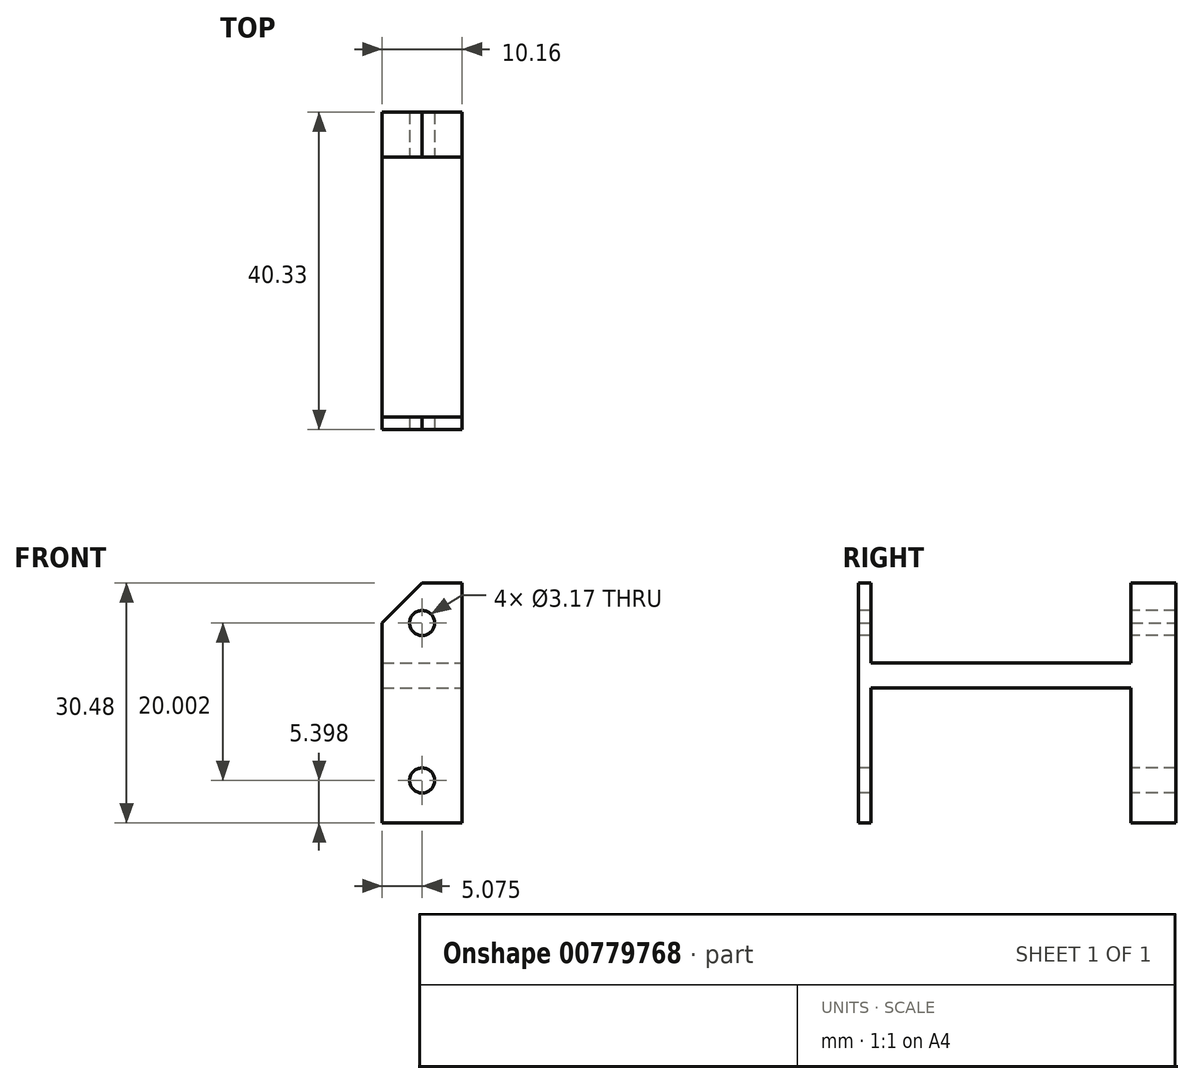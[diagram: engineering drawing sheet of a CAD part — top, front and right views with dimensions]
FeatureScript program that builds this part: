
annotation { "Feature Type Name" : "Feature", "Feature Type Description" : "" }
export const myFeature = defineFeature(function(context is Context, id is Id, definition is map)
    precondition{}
    {
        {
            var Q0;
            Q0=qCreatedBy(makeId("Front.planeOp"),FACE);
            var sketch = newSketch(context, id + "F0", { "sketchPlane" : qUnion([Q0])});
            skLineSegment(sketch, "E0", {"start": v(-16.21, 9.2) * mm, "end": v(-16.21, -16.2) * mm});
            skLineSegment(sketch, "E1", {"start": v(-16.21, -16.2) * mm, "end": v(-6.05, -16.2) * mm});
            skLineSegment(sketch, "E2", {"start": v(-6.05, -16.2) * mm, "end": v(-6.05, 14.27) * mm});
            skLineSegment(sketch, "E3", {"start": v(-6.05, 14.27) * mm, "end": v(-11.13, 14.27) * mm});
            skLineSegment(sketch, "E4", {"start": v(-11.13, 14.27) * mm, "end": v(-16.21, 9.2) * mm});
            skSolve(sketch);
        }
        {
            var Q0;
            Q0=makeQuery(id+"F0.imprint","IMPRINT",FACE,{"disambiguationData":[TD([[makeQuery(id+"F0.imprint","IMPRINT",EDGE,{"derivedFrom":sQuery(id+"F0.wireOp",EDGE,"E0")}),1.0]])]});
            extrude(context, id + "F1", {"entities" : qUnion([Q0]), "depth" : 1.59 * mm, "offsetDistance" : 25.4 * mm});
        }
        {
            var Q0;
            Q0=makeQuery(id+"F1.opExtrude","CAP_FACE",FACE,{"disambiguationData":[OSD([sQuery(id+"F0.wireOp",EDGE,"E0"),sQuery(id+"F0.wireOp",EDGE,"E1"),sQuery(id+"F0.wireOp",EDGE,"E2"),sQuery(id+"F0.wireOp",EDGE,"E3"),sQuery(id+"F0.wireOp",EDGE,"E4")])],"isStart":false});
            var sketch = newSketch(context, id + "F2", { "sketchPlane" : qUnion([Q0])});
            skLineSegment(sketch, "E5.bottom", {"start": v(-16.21, 4.11) * mm, "end": v(-6.05, 4.11) * mm});
            skLineSegment(sketch, "E5.top", {"start": v(-16.21, 0.94) * mm, "end": v(-6.05, 0.94) * mm});
            skLineSegment(sketch, "E5.left", {"start": v(-16.21, 4.11) * mm, "end": v(-16.21, 0.94) * mm});
            skLineSegment(sketch, "E5.right", {"start": v(-6.05, 4.11) * mm, "end": v(-6.05, 0.94) * mm});
            skSolve(sketch);
        }
        {
            var Q0;
            Q0=makeQuery(id+"F2.imprint","IMPRINT",FACE,{"disambiguationData":[TD([[makeQuery(id+"F2.imprint","IMPRINT",EDGE,{"derivedFrom":sQuery(id+"F2.wireOp",EDGE,"E5.bottom")}),-1.0]])]});
            extrude(context, id + "F3", {"entities" : qUnion([Q0]), "operationType" : NewBodyOperationType.ADD, "depth" : 33.02 * mm, "offsetDistance" : 25.4 * mm});
        }
        {
            var Q0;
            Q0=makeQuery(id+"F3.opExtrude","CAP_FACE",FACE,{"disambiguationData":[OSD([sQuery(id+"F2.wireOp",EDGE,"E5.bottom"),sQuery(id+"F2.wireOp",EDGE,"E5.top"),sQuery(id+"F2.wireOp",EDGE,"E5.left"),sQuery(id+"F2.wireOp",EDGE,"E5.right")])],"isStart":false});
            var sketch = newSketch(context, id + "F4", { "sketchPlane" : qUnion([Q0])});
            skLineSegment(sketch, "E6", {"start": v(-16.21, 4.11) * mm, "end": v(-16.21, 0.94) * mm});
            skLineSegment(sketch, "E7", {"start": v(-16.21, 0.94) * mm, "end": v(-16.21, -16.2) * mm});
            skLineSegment(sketch, "E8", {"start": v(-16.21, -16.2) * mm, "end": v(-6.05, -16.2) * mm});
            skLineSegment(sketch, "E9", {"start": v(-6.05, -16.2) * mm, "end": v(-6.05, 0.94) * mm});
            skLineSegment(sketch, "E10", {"start": v(-6.05, 0.94) * mm, "end": v(-6.05, 4.11) * mm});
            skLineSegment(sketch, "E11", {"start": v(-6.05, 4.11) * mm, "end": v(-6.05, 14.27) * mm});
            skLineSegment(sketch, "E12", {"start": v(-6.05, 14.27) * mm, "end": v(-11.13, 14.27) * mm});
            skLineSegment(sketch, "E13", {"start": v(-11.13, 14.27) * mm, "end": v(-16.21, 9.2) * mm});
            skLineSegment(sketch, "E14", {"start": v(-16.21, 9.2) * mm, "end": v(-16.21, 4.11) * mm});
            skSolve(sketch);
        }
        {
            var Q0;
            Q0 = qSketchRegion(id + "F4", true);
            extrude(context, id + "F5", {"entities" : qUnion([Q0]), "operationType" : NewBodyOperationType.ADD, "depth" : 1.59 * mm, "offsetDistance" : 25.4 * mm});
        }
        {
            var Q0;
            Q0=makeQuery(id+"F1.opExtrude","CAP_FACE",FACE,{"disambiguationData":[OSD([sQuery(id+"F0.wireOp",EDGE,"E0"),sQuery(id+"F0.wireOp",EDGE,"E1"),sQuery(id+"F0.wireOp",EDGE,"E2"),sQuery(id+"F0.wireOp",EDGE,"E3"),sQuery(id+"F0.wireOp",EDGE,"E4")])],"isStart":true});
            var sketch = newSketch(context, id + "F6", { "sketchPlane" : qUnion([Q0])});
            skLineSegment(sketch, "E15.bottom", {"start": v(16.21, -16.2) * mm, "end": v(6.05, -16.2) * mm});
            skLineSegment(sketch, "E15.top", {"start": v(16.21, -39.07) * mm, "end": v(6.05, -39.07) * mm});
            skLineSegment(sketch, "E15.left", {"start": v(6.05, -16.2) * mm, "end": v(6.05, -39.07) * mm});
            skLineSegment(sketch, "E15.right", {"start": v(16.21, -16.2) * mm, "end": v(16.21, -39.07) * mm});
            skSolve(sketch);
        }
        {
            var Q0;
            Q0=makeQuery(id+"F6.imprint","IMPRINT",FACE,{"disambiguationData":[TD([[makeQuery(id+"F6.imprint","IMPRINT",EDGE,{"derivedFrom":sQuery(id+"F6.wireOp",EDGE,"E15.bottom")}),-1.0]])]});
            extrude(context, id + "F7", {"entities" : qUnion([Q0]), "operationType" : NewBodyOperationType.ADD, "depth" : 4.13 * mm, "offsetDistance" : 25.4 * mm});
        }
        {
            var Q0;
            Q0=makeQuery(id+"F5.opExtrude","CAP_FACE",FACE,{"disambiguationData":[OSD([sQuery(id+"F4.wireOp",EDGE,"E6"),sQuery(id+"F4.wireOp",EDGE,"E7"),sQuery(id+"F4.wireOp",EDGE,"E8"),sQuery(id+"F4.wireOp",EDGE,"E9"),sQuery(id+"F4.wireOp",EDGE,"E10"),sQuery(id+"F4.wireOp",EDGE,"E11"),sQuery(id+"F4.wireOp",EDGE,"E12"),sQuery(id+"F4.wireOp",EDGE,"E13"),sQuery(id+"F4.wireOp",EDGE,"E14")])],"isStart":false});
            var sketch = newSketch(context, id + "F8", { "sketchPlane" : qUnion([Q0])});
            skCircle(sketch, "E16", {"center": v(-11.13, -10.81) * mm, "radius": 1.59 * mm});
            skPoint(sketch, "E16.centerSnap0", {"position": v(-11.13, -16.2) * mm});
            skSolve(sketch);
        }
        {
            var Q0;
            Q0=makeQuery(id+"F8.imprint","IMPRINT",FACE,{"disambiguationData":[TD([[makeQuery(id+"F8.imprint","IMPRINT",EDGE,{"derivedFrom":sQuery(id+"F8.wireOp",EDGE,"E16")}),1.0]])]});
            extrude(context, id + "F9", {"entities" : qUnion([Q0]), "operationType" : NewBodyOperationType.REMOVE, "oppositeDirection" : true, "depth" : 50.8 * mm, "offsetDistance" : 25.4 * mm});
        }
        {
            var Q0;
            Q0=makeQuery(id+"F5.opExtrude","CAP_FACE",FACE,{"disambiguationData":[OSD([sQuery(id+"F4.wireOp",EDGE,"E6"),sQuery(id+"F4.wireOp",EDGE,"E7"),sQuery(id+"F4.wireOp",EDGE,"E8"),sQuery(id+"F4.wireOp",EDGE,"E9"),sQuery(id+"F4.wireOp",EDGE,"E10"),sQuery(id+"F4.wireOp",EDGE,"E11"),sQuery(id+"F4.wireOp",EDGE,"E12"),sQuery(id+"F4.wireOp",EDGE,"E13"),sQuery(id+"F4.wireOp",EDGE,"E14")])],"isStart":false});
            var sketch = newSketch(context, id + "F10", { "sketchPlane" : qUnion([Q0])});
            skCircle(sketch, "E17", {"center": v(-11.13, 9.2) * mm, "radius": 1.59 * mm});
            skSolve(sketch);
        }
        {
            var Q0;
            Q0=makeQuery(id+"F10.imprint","IMPRINT",FACE,{"disambiguationData":[TD([[makeQuery(id+"F10.imprint","IMPRINT",EDGE,{"derivedFrom":sQuery(id+"F10.wireOp",EDGE,"E17")}),1.0]])]});
            extrude(context, id + "F11", {"entities" : qUnion([Q0]), "operationType" : NewBodyOperationType.REMOVE, "oppositeDirection" : true, "depth" : 50.8 * mm, "offsetDistance" : 25.4 * mm});
        }
    });
